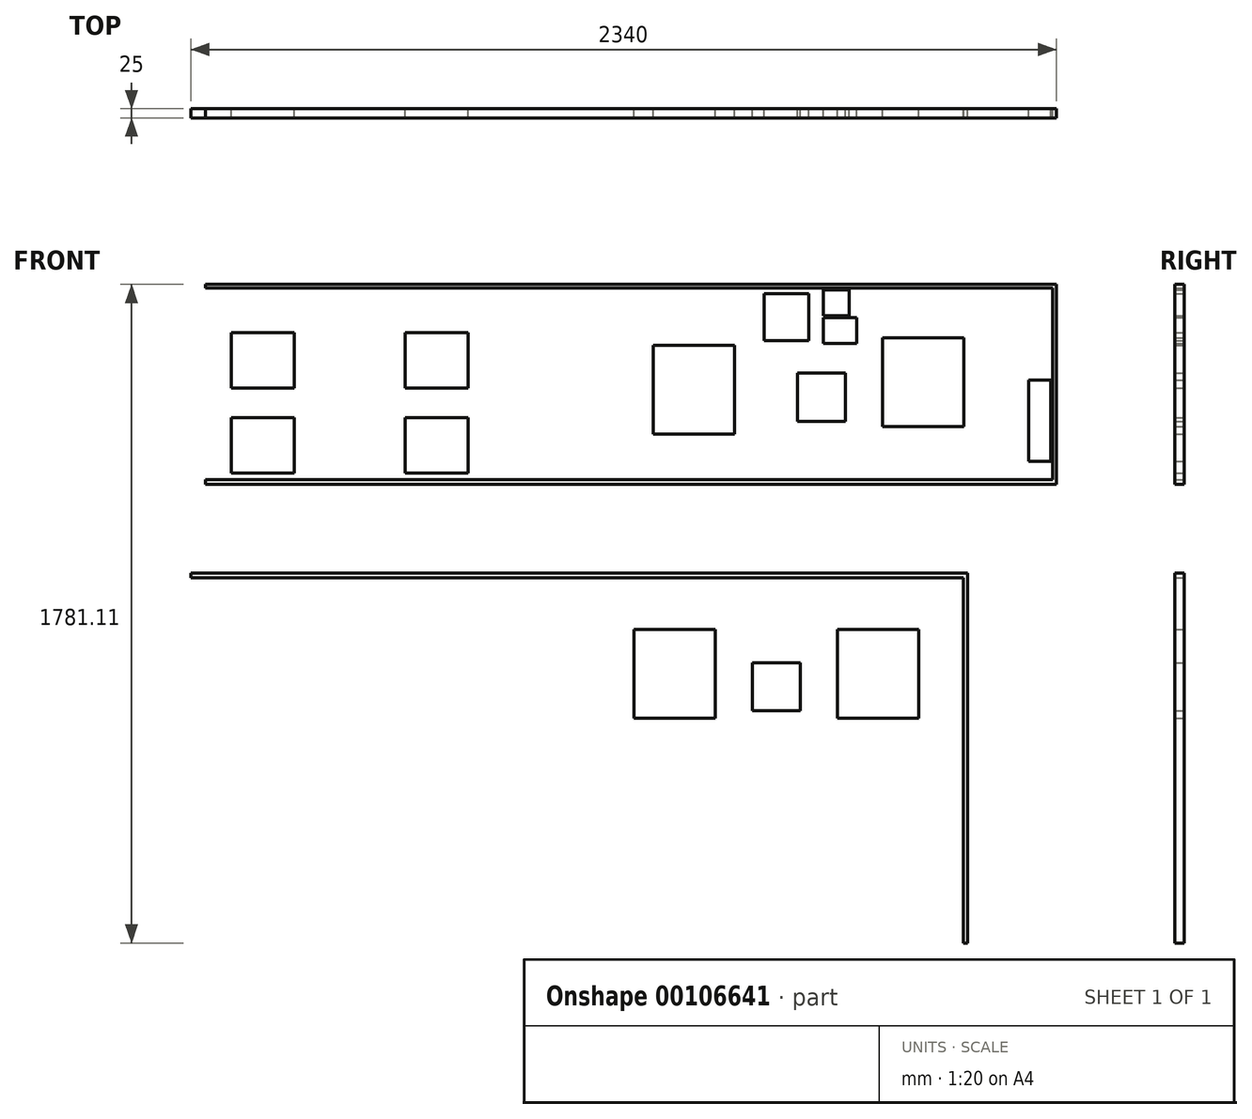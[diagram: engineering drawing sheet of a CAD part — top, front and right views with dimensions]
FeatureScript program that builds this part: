
annotation { "Feature Type Name" : "Feature", "Feature Type Description" : "" }
export const myFeature = defineFeature(function(context is Context, id is Id, definition is map)
    precondition{}
    {
        {
            var Q0;
            Q0=qCreatedBy(makeId("Front.planeOp"),FACE);
            var sketch = newSketch(context, id + "F0", { "sketchPlane" : qUnion([Q0])});
            skLineSegment(sketch, "E0.bottom", {"start": v(220, -120) * mm, "end": v(0, -120) * mm});
            skLineSegment(sketch, "E0.top", {"start": v(220, 120) * mm, "end": v(0, 120) * mm});
            skLineSegment(sketch, "E0.left", {"start": v(220, -120) * mm, "end": v(220, 120) * mm});
            skLineSegment(sketch, "E0.right", {"start": v(0, -120) * mm, "end": v(0, 120) * mm});
            skPoint(sketch, "E0.middle", {"position": v(110, 0) * mm});
            skLineSegment(sketch, "E1.bottom", {"start": v(470, 255) * mm, "end": v(-1830, 255) * mm});
            skLineSegment(sketch, "E1.top", {"start": v(470, 265) * mm, "end": v(-1830, 265) * mm});
            skLineSegment(sketch, "E1.left", {"start": v(470, 255) * mm, "end": v(470, 265) * mm});
            skLineSegment(sketch, "E1.right", {"start": v(-1830, 255) * mm, "end": v(-1830, 265) * mm});
            skLineSegment(sketch, "E2.bottom", {"start": v(-230, 25) * mm, "end": v(-100, 25) * mm});
            skLineSegment(sketch, "E2.top", {"start": v(-230, -105) * mm, "end": v(-100, -105) * mm});
            skLineSegment(sketch, "E2.left", {"start": v(-230, 25) * mm, "end": v(-230, -105) * mm});
            skLineSegment(sketch, "E2.right", {"start": v(-100, 25) * mm, "end": v(-100, -105) * mm});
            skLineSegment(sketch, "E3.bottom", {"start": v(-320, 240) * mm, "end": v(-200, 240) * mm});
            skLineSegment(sketch, "E3.top", {"start": v(-320, 113) * mm, "end": v(-200, 113) * mm});
            skLineSegment(sketch, "E3.left", {"start": v(-320, 240) * mm, "end": v(-320, 113) * mm});
            skLineSegment(sketch, "E3.right", {"start": v(-200, 240) * mm, "end": v(-200, 113) * mm});
            skLineSegment(sketch, "E4.bottom", {"start": v(-160, 175) * mm, "end": v(-70, 175) * mm});
            skLineSegment(sketch, "E4.top", {"start": v(-160, 105) * mm, "end": v(-70, 105) * mm});
            skLineSegment(sketch, "E4.left", {"start": v(-160, 175) * mm, "end": v(-160, 105) * mm});
            skLineSegment(sketch, "E4.right", {"start": v(-70, 175) * mm, "end": v(-70, 105) * mm});
            skLineSegment(sketch, "E5.bottom", {"start": v(-160, 250) * mm, "end": v(-90, 250) * mm});
            skLineSegment(sketch, "E5.top", {"start": v(-160, 180) * mm, "end": v(-90, 180) * mm});
            skLineSegment(sketch, "E5.left", {"start": v(-160, 250) * mm, "end": v(-160, 180) * mm});
            skLineSegment(sketch, "E5.right", {"start": v(-90, 250) * mm, "end": v(-90, 180) * mm});
            skLineSegment(sketch, "E6.bottom", {"start": v(-1830, -263.4) * mm, "end": v(470, -263.4) * mm});
            skLineSegment(sketch, "E6.top", {"start": v(-1830, -276.11) * mm, "end": v(470, -276.11) * mm});
            skLineSegment(sketch, "E6.left", {"start": v(-1830, -263.4) * mm, "end": v(-1830, -276.11) * mm});
            skLineSegment(sketch, "E6.right", {"start": v(470, -263.4) * mm, "end": v(470, -276.11) * mm});
            skLineSegment(sketch, "E7.bottom", {"start": v(470, 265) * mm, "end": v(460, 265) * mm});
            skLineSegment(sketch, "E7.top", {"start": v(470, -276.11) * mm, "end": v(460, -276.11) * mm});
            skLineSegment(sketch, "E7.left", {"start": v(470, 265) * mm, "end": v(470, -276.11) * mm});
            skLineSegment(sketch, "E7.right", {"start": v(460, 265) * mm, "end": v(460, -276.11) * mm});
            skLineSegment(sketch, "E8.bottom", {"start": v(395, 6.6) * mm, "end": v(455, 6.6) * mm});
            skLineSegment(sketch, "E8.top", {"start": v(395, -213.4) * mm, "end": v(455, -213.4) * mm});
            skLineSegment(sketch, "E8.left", {"start": v(395, 6.6) * mm, "end": v(395, -213.4) * mm});
            skLineSegment(sketch, "E8.right", {"start": v(455, 6.6) * mm, "end": v(455, -213.4) * mm});
            skLineSegment(sketch, "E9.bottom", {"start": v(-400, -140) * mm, "end": v(-620, -140) * mm});
            skLineSegment(sketch, "E9.top", {"start": v(-400, 100) * mm, "end": v(-620, 100) * mm});
            skLineSegment(sketch, "E9.left", {"start": v(-400, -140) * mm, "end": v(-400, 100) * mm});
            skLineSegment(sketch, "E9.right", {"start": v(-620, -140) * mm, "end": v(-620, 100) * mm});
            skLineSegment(sketch, "E10.bottom", {"start": v(-1290, 135) * mm, "end": v(-1120, 135) * mm});
            skLineSegment(sketch, "E10.top", {"start": v(-1290, -15) * mm, "end": v(-1120, -15) * mm});
            skLineSegment(sketch, "E10.left", {"start": v(-1290, 135) * mm, "end": v(-1290, -15) * mm});
            skLineSegment(sketch, "E10.right", {"start": v(-1120, 135) * mm, "end": v(-1120, -15) * mm});
            skLineSegment(sketch, "E11.bottom", {"start": v(-1290, -95) * mm, "end": v(-1120, -95) * mm});
            skLineSegment(sketch, "E11.top", {"start": v(-1290, -245) * mm, "end": v(-1120, -245) * mm});
            skLineSegment(sketch, "E11.left", {"start": v(-1290, -95) * mm, "end": v(-1290, -245) * mm});
            skLineSegment(sketch, "E11.right", {"start": v(-1120, -95) * mm, "end": v(-1120, -245) * mm});
            skLineSegment(sketch, "E12.bottom", {"start": v(230, -516.11) * mm, "end": v(-1870, -516.11) * mm});
            skLineSegment(sketch, "E12.top", {"start": v(230, -528.11) * mm, "end": v(-1870, -528.11) * mm});
            skLineSegment(sketch, "E12.left", {"start": v(230, -516.11) * mm, "end": v(230, -528.11) * mm});
            skLineSegment(sketch, "E12.right", {"start": v(-1870, -516.11) * mm, "end": v(-1870, -528.11) * mm});
            skLineSegment(sketch, "E13.bottom", {"start": v(230, -516.11) * mm, "end": v(218, -516.11) * mm});
            skLineSegment(sketch, "E13.top", {"start": v(230, -1516.11) * mm, "end": v(218, -1516.11) * mm});
            skLineSegment(sketch, "E13.left", {"start": v(230, -516.11) * mm, "end": v(230, -1516.11) * mm});
            skLineSegment(sketch, "E13.right", {"start": v(218, -516.11) * mm, "end": v(218, -1516.11) * mm});
            skLineSegment(sketch, "E14.bottom", {"start": v(-452, -908.11) * mm, "end": v(-672, -908.11) * mm});
            skLineSegment(sketch, "E14.top", {"start": v(-452, -668.11) * mm, "end": v(-672, -668.11) * mm});
            skLineSegment(sketch, "E14.left", {"start": v(-452, -908.11) * mm, "end": v(-452, -668.11) * mm});
            skLineSegment(sketch, "E14.right", {"start": v(-672, -908.11) * mm, "end": v(-672, -668.11) * mm});
            skLineSegment(sketch, "E15.bottom", {"start": v(98, -908.11) * mm, "end": v(-122, -908.11) * mm});
            skLineSegment(sketch, "E15.top", {"start": v(98, -668.11) * mm, "end": v(-122, -668.11) * mm});
            skLineSegment(sketch, "E15.left", {"start": v(98, -908.11) * mm, "end": v(98, -668.11) * mm});
            skLineSegment(sketch, "E15.right", {"start": v(-122, -908.11) * mm, "end": v(-122, -668.11) * mm});
            skLineSegment(sketch, "E16.bottom", {"start": v(-352, -758.11) * mm, "end": v(-222, -758.11) * mm});
            skLineSegment(sketch, "E16.top", {"start": v(-352, -888.11) * mm, "end": v(-222, -888.11) * mm});
            skLineSegment(sketch, "E16.left", {"start": v(-352, -758.11) * mm, "end": v(-352, -888.11) * mm});
            skLineSegment(sketch, "E16.right", {"start": v(-222, -758.11) * mm, "end": v(-222, -888.11) * mm});
            skLineSegment(sketch, "E17.bottom", {"start": v(-1760, 135) * mm, "end": v(-1590, 135) * mm});
            skLineSegment(sketch, "E17.top", {"start": v(-1760, -15) * mm, "end": v(-1590, -15) * mm});
            skLineSegment(sketch, "E17.left", {"start": v(-1760, 135) * mm, "end": v(-1760, -15) * mm});
            skLineSegment(sketch, "E17.right", {"start": v(-1590, 135) * mm, "end": v(-1590, -15) * mm});
            skLineSegment(sketch, "E18.bottom", {"start": v(-1760, -95) * mm, "end": v(-1590, -95) * mm});
            skLineSegment(sketch, "E18.top", {"start": v(-1760, -245) * mm, "end": v(-1590, -245) * mm});
            skLineSegment(sketch, "E18.left", {"start": v(-1760, -95) * mm, "end": v(-1760, -245) * mm});
            skLineSegment(sketch, "E18.right", {"start": v(-1590, -95) * mm, "end": v(-1590, -245) * mm});
            skSolve(sketch);
        }
        {
            var Q0;
            Q0=qSketchRegion(id+"F0",true);
            extrude(context, id + "F1", {"entities" : qUnion([Q0]), "depth" : 25 * mm});
        }
    });
